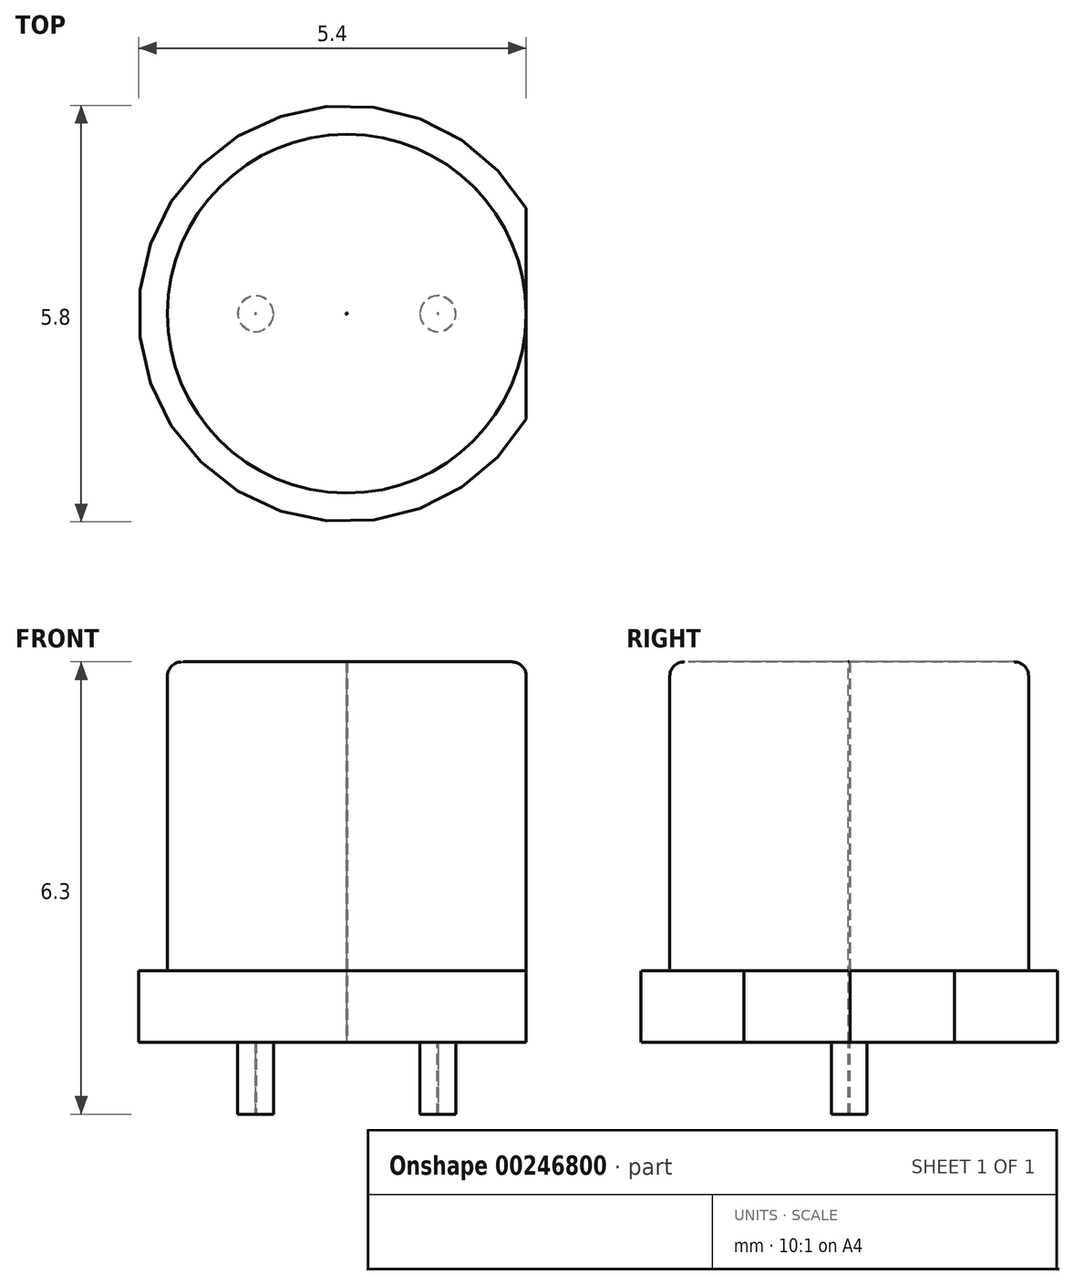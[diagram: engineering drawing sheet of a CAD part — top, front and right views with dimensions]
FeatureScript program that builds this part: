
annotation { "Feature Type Name" : "Feature", "Feature Type Description" : "" }
export const myFeature = defineFeature(function(context is Context, id is Id, definition is map)
    precondition{}
    {
        {
            var Q0;
            Q0=qCreatedBy(makeId("Front.planeOp"),FACE);
            var sketch = newSketch(context, id + "F0", { "sketchPlane" : qUnion([Q0])});
            skLineSegment(sketch, "E0", {"start": v(0, 0) * mm, "end": v(0, 4.3) * mm});
            skLineSegment(sketch, "E1", {"start": v(0, 4.3) * mm, "end": v(2.5, 4.3) * mm});
            skLineSegment(sketch, "E2", {"start": v(2.5, 4.3) * mm, "end": v(2.5, 0) * mm});
            skLineSegment(sketch, "E3", {"start": v(2.5, 0) * mm, "end": v(0, 0) * mm});
            skLineSegment(sketch, "E4", {"start": v(0, 0) * mm, "end": v(0, -1) * mm});
            skLineSegment(sketch, "E5", {"start": v(0, -1) * mm, "end": v(2.9, -1) * mm});
            skLineSegment(sketch, "E6", {"start": v(2.9, -1) * mm, "end": v(2.9, 0) * mm});
            skLineSegment(sketch, "E7", {"start": v(2.9, 0) * mm, "end": v(2.5, 0) * mm});
            skLineSegment(sketch, "E8", {"start": v(1.27, -1) * mm, "end": v(1.27, -27.2) * mm});
            skLineSegment(sketch, "E9", {"start": v(1.27, -27.2) * mm, "end": v(1.52, -27.2) * mm});
            skLineSegment(sketch, "E10", {"start": v(1.52, -27.2) * mm, "end": v(1.52, -1) * mm, "construction": true});
            skLineSegment(sketch, "E11", {"start": v(1.27, -27.2) * mm, "end": v(1.02, -27.2) * mm});
            skLineSegment(sketch, "E12", {"start": v(1.02, -27.2) * mm, "end": v(1.02, -1) * mm});
            skLineSegment(sketch, "E13.MirrorCS", {"start": v(-1.02, -27.2) * mm, "end": v(-1.02, -1) * mm});
            skLineSegment(sketch, "E14", {"start": v(-1.27, -1) * mm, "end": v(-1.02, -1) * mm});
            skLineSegment(sketch, "E15", {"start": v(-1.27, -29.7) * mm, "end": v(-1.02, -29.7) * mm});
            skLineSegment(sketch, "E16", {"start": v(-1.02, -29.7) * mm, "end": v(-1.02, -27.2) * mm});
            skLineSegment(sketch, "E17", {"start": v(-1.27, -29.7) * mm, "end": v(-1.27, -1) * mm});
            skSolve(sketch);
        }
        {
            var Q0;
            Q0=makeQuery(id+"F0.imprint","IMPRINT",FACE,{"disambiguationData":[TD([[makeQuery(id+"F0.imprint","IMPRINT",EDGE,{"derivedFrom":sQuery(id+"F0.wireOp",EDGE,"E0")}),-1.0]])]});
            var Q1;
            Q1=makeQuery(id+"F0.imprint","IMPRINT",FACE,{"disambiguationData":[TD([[makeQuery(id+"F0.imprint","IMPRINT",EDGE,{"derivedFrom":sQuery(id+"F0.wireOp",EDGE,"E3")}),1.0]])]});
            extrude(context, id + "F1", {"entities" : qUnion([Q0, Q1]), "depth" : 0.01 * mm});
        }
        {
            var Q0;
            Q0=makeQuery(id+"F1.opExtrude","CAP_FACE",FACE,{"disambiguationData":[OSD([sQuery(id+"F0.wireOp",EDGE,"E0"),sQuery(id+"F0.wireOp",EDGE,"E1"),sQuery(id+"F0.wireOp",EDGE,"E2"),sQuery(id+"F0.wireOp",EDGE,"E4"),sQuery(id+"F0.wireOp",EDGE,"E5"),sQuery(id+"F0.wireOp",EDGE,"E6"),sQuery(id+"F0.wireOp",EDGE,"E7")])],"isStart":false});
            var Q1;
            Q1=makeQuery(id+"F1.opExtrude","CAP_EDGE",EDGE,{"disambiguationData":[OSD([sQuery(id+"F0.wireOp",EDGE,"E0"),sQuery(id+"F0.wireOp",EDGE,"E4")])],"isStart":true});
            revolve(context, id + "F2", {"operationType" : NewBodyOperationType.ADD, "entities" : qUnion([Q0]), "axis" : qUnion([Q1]), "revolveType" : RevolveType.FULL});
        }
        {
            var Q0;
            Q0=qCreatedBy(makeId("Right.planeOp"),FACE);
            cPlane(context, id + "F3", {"entities" : qUnion([Q0]), "cplaneType" : CPlaneType.OFFSET, "offset" : 2.5 * mm, "width" : 150 * mm, "height" : 150 * mm});
        }
        {
            var Q0;
            Q0=qCreatedBy(id+"F3.planeOp",FACE);
            var sketch = newSketch(context, id + "F4", { "sketchPlane" : qUnion([Q0])});
            skLineSegment(sketch, "E18.bottom", {"start": v(1.5, -1.2) * mm, "end": v(-1.5, -1.2) * mm});
            skLineSegment(sketch, "E18.top", {"start": v(1.5, 1.2) * mm, "end": v(-1.5, 1.2) * mm});
            skLineSegment(sketch, "E18.left", {"start": v(1.5, -1.2) * mm, "end": v(1.5, 1.2) * mm});
            skLineSegment(sketch, "E18.right", {"start": v(-1.5, -1.2) * mm, "end": v(-1.5, 1.2) * mm});
            skPoint(sketch, "E18.middle", {"position": v(0, 0) * mm});
            skSolve(sketch);
        }
        {
            var Q0;
            Q0=qSketchRegion(id+"F4",true);
            extrude(context, id + "F5", {"entities" : qUnion([Q0]), "operationType" : NewBodyOperationType.REMOVE, "depth" : 2 * mm});
        }
        {
            var Q0;
            {var subQ0=sQuery(id+"F0.wireOp",EDGE,"E8");Q0=makeQuery(id+"F0.imprint","IMPRINT",FACE,{"disambiguationData":[TD([[makeQuery(id+"F0.imprint","IMPRINT",EDGE,{"derivedFrom":subQ0}),-1.0]])]});}
            extrude(context, id + "F6", {"entities" : qUnion([Q0]), "operationType" : NewBodyOperationType.ADD, "depth" : 0.01 * mm});
        }
        {
            var Q0;
            Q0=makeQuery(id+"F0.imprint","IMPRINT",FACE,{"disambiguationData":[TD([[makeQuery(id+"F0.imprint","IMPRINT",EDGE,{"derivedFrom":sQuery(id+"F0.wireOp",EDGE,"E13.MirrorCS")}),1.0]])]});
            extrude(context, id + "F7", {"entities" : qUnion([Q0]), "operationType" : NewBodyOperationType.ADD, "depth" : 0.01 * mm});
        }
        {
            var Q0;
            Q0=makeQuery(id+"F7.opExtrude","CAP_FACE",FACE,{"disambiguationData":[OSD([sQuery(id+"F0.wireOp",EDGE,"E13.MirrorCS"),sQuery(id+"F0.wireOp",EDGE,"ac1886b3-cde3-48e8-9153-fe326fcb880c0.MirrorCS"),sQuery(id+"F0.wireOp",EDGE,"E14"),sQuery(id+"F0.wireOp",EDGE,"SvBCKN1I-MjCF-pU42-bqUf-L1uZbrdVZMYg"),sQuery(id+"F0.wireOp",EDGE,"E15"),sQuery(id+"F0.wireOp",EDGE,"E16")])],"isStart":false});
            var Q1;
            Q1=sQuery(id+"F0.wireOp",EDGE,"E17");
            revolve(context, id + "F8", {"operationType" : NewBodyOperationType.ADD, "entities" : qUnion([Q0]), "axis" : qUnion([Q1]), "revolveType" : RevolveType.FULL});
        }
        {
            var Q0;
            Q0=makeQuery(id+"F6.opExtrude","CAP_FACE",FACE,{"disambiguationData":[OSD([sQuery(id+"F0.wireOp",EDGE,"E5"),sQuery(id+"F0.wireOp",EDGE,"E8"),sQuery(id+"F0.wireOp",EDGE,"E11"),sQuery(id+"F0.wireOp",EDGE,"E12")])],"isStart":false});
            var Q1;
            Q1=sQuery(id+"F0.wireOp",EDGE,"E8");
            revolve(context, id + "F9", {"operationType" : NewBodyOperationType.ADD, "entities" : qUnion([Q0]), "axis" : qUnion([Q1]), "revolveType" : RevolveType.FULL});
        }
        {
            var Q0;
            Q0=makeQuery(id+"F2.opRevolve","SWEPT_EDGE",EDGE,{"disambiguationData":[OSD([sQuery(id+"F0.wireOp",EDGE,"E1"),sQuery(id+"F0.wireOp",EDGE,"E2")])]});
            fillet(context, id + "F10", {"entities" : qUnion([Q0]), "radius" : 0.2 * mm, "tangentPropagation" : true, "allowEdgeOverflow" : false});
        }
        {
            var Q0;
            Q0=qCreatedBy(makeId("Front.planeOp"),FACE);
            var sketch = newSketch(context, id + "F11", { "sketchPlane" : qUnion([Q0])});
            skLineSegment(sketch, "E19.bottom", {"start": v(-17.34, -2) * mm, "end": v(20.66, -2) * mm});
            skLineSegment(sketch, "E19.top", {"start": v(-17.34, -35) * mm, "end": v(20.66, -35) * mm});
            skLineSegment(sketch, "E19.left", {"start": v(-17.34, -2) * mm, "end": v(-17.34, -35) * mm});
            skLineSegment(sketch, "E19.right", {"start": v(20.66, -2) * mm, "end": v(20.66, -35) * mm});
            skSolve(sketch);
        }
        {
            var Q0;
            Q0=qSketchRegion(id+"F11",true);
            extrude(context, id + "F12", {"entities" : qUnion([Q0]), "operationType" : NewBodyOperationType.REMOVE, "endBound" : BoundingType.SYMMETRIC, "oppositeDirection" : true, "depth" : 25 * mm});
        }
    });
